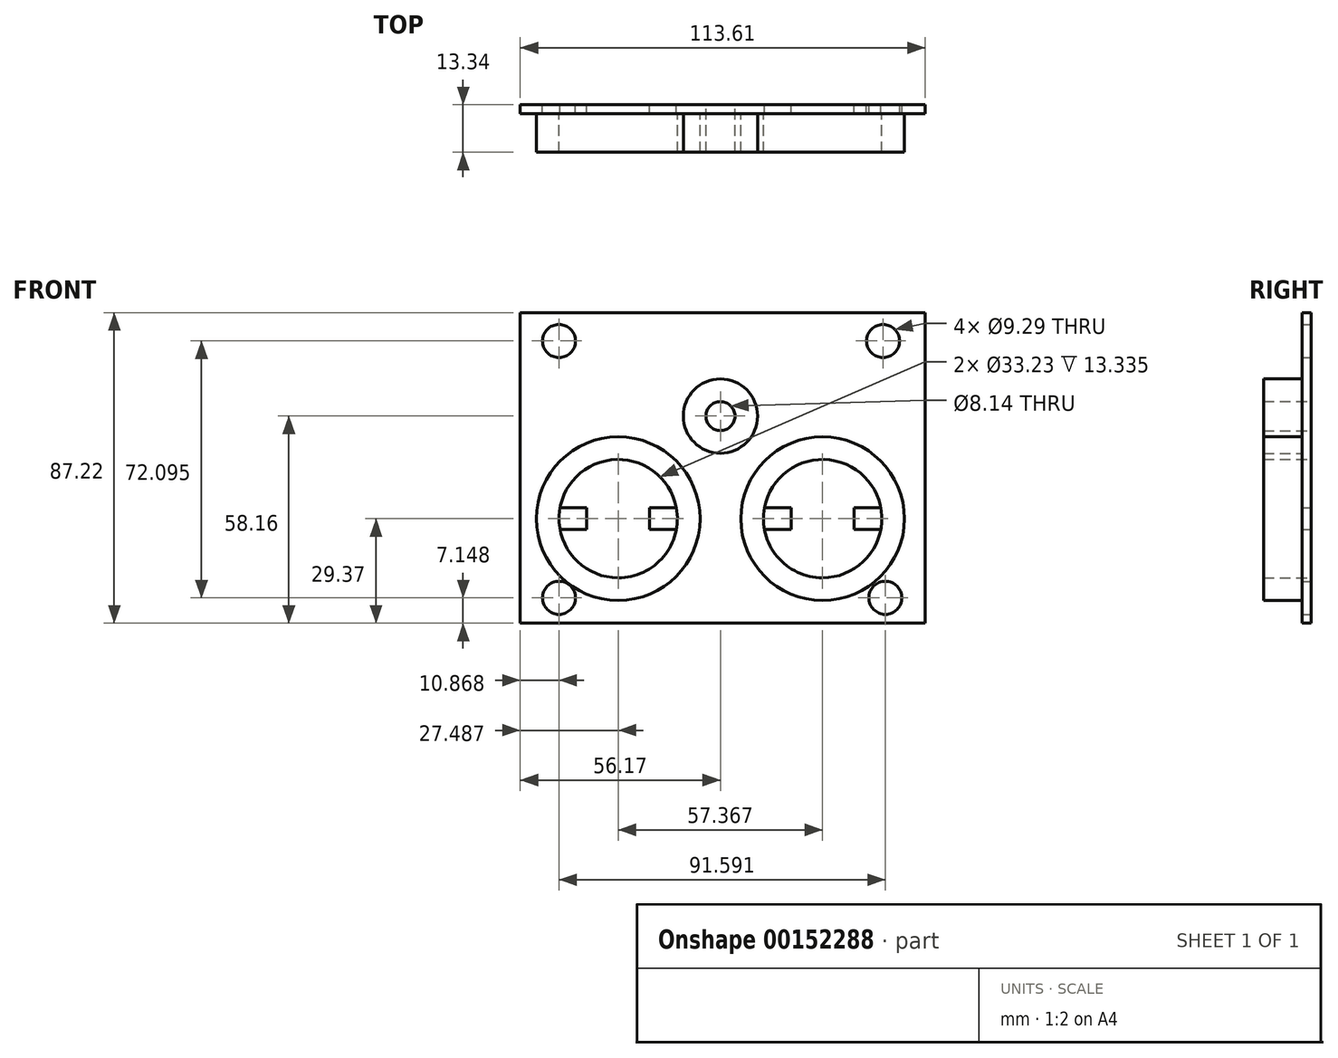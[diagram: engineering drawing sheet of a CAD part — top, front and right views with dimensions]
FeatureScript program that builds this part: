
annotation { "Feature Type Name" : "Feature", "Feature Type Description" : "" }
export const myFeature = defineFeature(function(context is Context, id is Id, definition is map)
    precondition{}
    {
        {
            var Q0;
            Q0=qCreatedBy(makeId("Front.planeOp"),FACE);
            cPlane(context, id + "F0", {"entities" : qUnion([Q0]), "cplaneType" : CPlaneType.OFFSET, "offset" : 76.2 * mm, "width" : 152.4 * mm, "height" : 152.4 * mm});
        }
        {
            var Q0;
            Q0=qCreatedBy(id+"F0.planeOp",FACE);
            var sketch = newSketch(context, id + "F1", { "sketchPlane" : qUnion([Q0])});
            skCircle(sketch, "E0", {"center": v(-28.68, 0) * mm, "radius": 20.32 * mm, "construction": true});
            skCircle(sketch, "E1", {"center": v(0, 28.8) * mm, "radius": 20.32 * mm, "construction": true});
            skCircle(sketch, "E2", {"center": v(28.68, 0) * mm, "radius": 20.32 * mm, "construction": true});
            skLineSegment(sketch, "E3.bottom", {"start": v(-56.17, 57.85) * mm, "end": v(57.44, 57.85) * mm});
            skLineSegment(sketch, "E3.top", {"start": v(-56.17, -29.37) * mm, "end": v(57.44, -29.37) * mm});
            skLineSegment(sketch, "E3.left", {"start": v(-56.17, 57.85) * mm, "end": v(-56.17, -29.37) * mm});
            skLineSegment(sketch, "E3.right", {"start": v(57.44, 57.85) * mm, "end": v(57.44, -29.37) * mm});
            skCircle(sketch, "E4", {"center": v(28.68, 0) * mm, "radius": 16.61 * mm});
            skCircle(sketch, "E5", {"center": v(-28.68, 0) * mm, "radius": 16.61 * mm});
            skCircle(sketch, "E6", {"center": v(0, 28.8) * mm, "radius": 4.07 * mm});
            skCircle(sketch, "E7", {"center": v(-28.68, 0) * mm, "radius": 4.07 * mm});
            skCircle(sketch, "E8", {"center": v(28.68, 0) * mm, "radius": 4.07 * mm});
            skCircle(sketch, "E9", {"center": v(28.68, 0) * mm, "radius": 7.31 * mm});
            skCircle(sketch, "E10", {"center": v(-28.68, 0) * mm, "radius": 7.31 * mm});
            skCircle(sketch, "E11", {"center": v(-45.3, 49.87) * mm, "radius": 4.65 * mm});
            skCircle(sketch, "E12", {"center": v(45.64, 49.87) * mm, "radius": 4.65 * mm});
            skCircle(sketch, "E13", {"center": v(46.29, -22.22) * mm, "radius": 4.65 * mm});
            skCircle(sketch, "E14", {"center": v(-45.3, -22.22) * mm, "radius": 4.65 * mm});
            skLineSegment(sketch, "E15.bottom", {"start": v(37.53, 3.04) * mm, "end": v(45.02, 3.04) * mm});
            skLineSegment(sketch, "E15.top", {"start": v(37.53, -3.04) * mm, "end": v(45.02, -3.04) * mm});
            skLineSegment(sketch, "E15.left", {"start": v(37.53, 3.04) * mm, "end": v(37.53, -3.04) * mm});
            skLineSegment(sketch, "E16", {"start": v(37.53, 0) * mm, "end": v(28.68, 0) * mm, "construction": true});
            skLineSegment(sketch, "E17", {"start": v(28.68, 0) * mm, "end": v(28.68, 20.32) * mm, "construction": true});
            skLineSegment(sketch, "E18", {"start": v(0, 0) * mm, "end": v(0, 28.8) * mm, "construction": true});
            skLineSegment(sketch, "E19", {"start": v(-28.68, 0) * mm, "end": v(0, 0) * mm, "construction": true});
            skLineSegment(sketch, "E20", {"start": v(0, 0) * mm, "end": v(28.68, 0) * mm, "construction": true});
            skSolve(sketch);
        }
        {
            var Q0;
            Q0=qCreatedBy(makeId("Front.planeOp"),FACE);
            var sketch = newSketch(context, id + "F2", { "sketchPlane" : qUnion([Q0])});
            skLineSegment(sketch, "E21.bottom", {"start": v(-56.17, -29.37) * mm, "end": v(57.44, -29.37) * mm});
            skLineSegment(sketch, "E21.top", {"start": v(-56.17, 57.85) * mm, "end": v(57.44, 57.85) * mm});
            skLineSegment(sketch, "E21.left", {"start": v(-56.17, -29.37) * mm, "end": v(-56.17, 57.85) * mm});
            skLineSegment(sketch, "E21.right", {"start": v(57.44, -29.37) * mm, "end": v(57.44, 57.85) * mm});
            skCircle(sketch, "E22", {"center": v(-28.68, 0) * mm, "radius": 16.61 * mm});
            skCircle(sketch, "E23", {"center": v(28.68, 0) * mm, "radius": 16.61 * mm});
            skCircle(sketch, "E24", {"center": v(0, 28.8) * mm, "radius": 4.07 * mm});
            skCircle(sketch, "E25.0", {"center": v(-28.68, 0) * mm, "radius": 22.96 * mm});
            skCircle(sketch, "E26.0", {"center": v(0, 28.8) * mm, "radius": 10.42 * mm});
            skCircle(sketch, "E27.0", {"center": v(28.68, 0) * mm, "radius": 22.96 * mm});
            skCircle(sketch, "E28", {"center": v(45.64, 49.87) * mm, "radius": 4.65 * mm});
            skCircle(sketch, "E29", {"center": v(-45.3, 49.87) * mm, "radius": 4.65 * mm});
            skCircle(sketch, "E30", {"center": v(-45.3, -22.22) * mm, "radius": 4.65 * mm});
            skCircle(sketch, "E31", {"center": v(46.29, -22.22) * mm, "radius": 4.65 * mm});
            skSolve(sketch);
        }
        {
            var Q0;
            Q0=makeQuery(id+"F2.imprint","IMPRINT",FACE,{"disambiguationData":[TD([[makeQuery(id+"F2.imprint","IMPRINT",EDGE,{"derivedFrom":sQuery(id+"F2.wireOp",EDGE,"E21.bottom")}),1.0]])]});
            var Q1;
            Q1=makeQuery(id+"F2.imprint","IMPRINT",FACE,{"disambiguationData":[TD([[makeQuery(id+"F2.imprint","IMPRINT",EDGE,{"derivedFrom":sQuery(id+"F2.wireOp",EDGE,"E22")}),-1.0]])]});
            var Q2;
            Q2=makeQuery(id+"F2.imprint","IMPRINT",FACE,{"disambiguationData":[TD([[makeQuery(id+"F2.imprint","IMPRINT",EDGE,{"derivedFrom":sQuery(id+"F2.wireOp",EDGE,"E24")}),-1.0]])]});
            var Q3;
            Q3=makeQuery(id+"F2.imprint","IMPRINT",FACE,{"disambiguationData":[TD([[makeQuery(id+"F2.imprint","IMPRINT",EDGE,{"derivedFrom":sQuery(id+"F2.wireOp",EDGE,"E23")}),-1.0]])]});
            var Q4;
            Q4=sQuery(id+"F2.wireOp",EDGE,"E21.top");
            extrude(context, id + "F3", {"entities" : qUnion([Q0, Q1, Q2, Q3]), "surfaceEntities" : qUnion([Q4]), "depth" : 2.54 * mm});
        }
        {
            var Q0;
            Q0=makeQuery(id+"F2.imprint","IMPRINT",FACE,{"disambiguationData":[TD([[makeQuery(id+"F2.imprint","IMPRINT",EDGE,{"derivedFrom":sQuery(id+"F2.wireOp",EDGE,"E24")}),-1.0]])]});
            var Q1;
            Q1=makeQuery(id+"F2.imprint","IMPRINT",FACE,{"disambiguationData":[TD([[makeQuery(id+"F2.imprint","IMPRINT",EDGE,{"derivedFrom":sQuery(id+"F2.wireOp",EDGE,"E23")}),-1.0]])]});
            var Q2;
            Q2=makeQuery(id+"F2.imprint","IMPRINT",FACE,{"disambiguationData":[TD([[makeQuery(id+"F2.imprint","IMPRINT",EDGE,{"derivedFrom":sQuery(id+"F2.wireOp",EDGE,"E22")}),-1.0]])]});
            extrude(context, id + "F4", {"entities" : qUnion([Q0, Q1, Q2]), "operationType" : NewBodyOperationType.ADD, "depth" : 13.33 * mm});
        }
        {
            var Q0;
            Q0=makeQuery(id+"F3.opExtrude","CAP_FACE",FACE,{"disambiguationData":[OSD([sQuery(id+"F2.wireOp",EDGE,"E21.bottom"),sQuery(id+"F2.wireOp",EDGE,"E21.top"),sQuery(id+"F2.wireOp",EDGE,"E21.left"),sQuery(id+"F2.wireOp",EDGE,"E21.right"),sQuery(id+"F2.wireOp",EDGE,"E22"),sQuery(id+"F2.wireOp",EDGE,"E23"),sQuery(id+"F2.wireOp",EDGE,"E24"),sQuery(id+"F2.wireOp",EDGE,"E28"),sQuery(id+"F2.wireOp",EDGE,"E29"),sQuery(id+"F2.wireOp",EDGE,"E30"),sQuery(id+"F2.wireOp",EDGE,"E31")])],"isStart":true});
            var sketch = newSketch(context, id + "F5", { "sketchPlane" : qUnion([Q0])});
            skLineSegment(sketch, "E32.bottom", {"start": v(-19.84, 3.04) * mm, "end": v(-12.35, 3.04) * mm});
            skLineSegment(sketch, "E32.top", {"start": v(-19.84, -3.04) * mm, "end": v(-12.35, -3.04) * mm});
            skLineSegment(sketch, "E32.left", {"start": v(-37.53, 3.04) * mm, "end": v(-37.53, -3.04) * mm});
            skArc(sketch, "E33", {"start": v(-12.35, -3.04) * mm, "mid": v(-12.07, 0) * mm, "end": v(-12.35, 3.04) * mm});
            skArc(sketch, "E34.MirrorCS", {"start": v(-45.02, -3.04) * mm, "mid": v(-45.3, 0) * mm, "end": v(-45.02, 3.04) * mm});
            skLineSegment(sketch, "E35.MirrorCS", {"start": v(-37.53, 3.04) * mm, "end": v(-45.02, 3.04) * mm});
            skLineSegment(sketch, "E36.MirrorCS", {"start": v(-37.53, -3.04) * mm, "end": v(-45.02, -3.04) * mm});
            skLineSegment(sketch, "E37.MirrorCS", {"start": v(-19.84, 3.04) * mm, "end": v(-19.84, -3.04) * mm});
            skLineSegment(sketch, "E38.MirrorCS", {"start": v(37.53, 3.04) * mm, "end": v(37.53, -3.04) * mm});
            skLineSegment(sketch, "E39.MirrorCS", {"start": v(37.53, -3.04) * mm, "end": v(45.02, -3.04) * mm});
            skArc(sketch, "E40.MirrorCS", {"start": v(45.02, -3.04) * mm, "mid": v(45.3, 0) * mm, "end": v(45.02, 3.04) * mm});
            skArc(sketch, "E41.MirrorCS", {"start": v(12.35, -3.04) * mm, "mid": v(12.07, 0) * mm, "end": v(12.35, 3.04) * mm});
            skLineSegment(sketch, "E42.MirrorCS", {"start": v(19.84, 3.04) * mm, "end": v(19.84, -3.04) * mm});
            skLineSegment(sketch, "E43.MirrorCS", {"start": v(37.53, 3.04) * mm, "end": v(45.02, 3.04) * mm});
            skLineSegment(sketch, "E44.MirrorCS", {"start": v(19.84, 3.04) * mm, "end": v(12.35, 3.04) * mm});
            skLineSegment(sketch, "E45.MirrorCS", {"start": v(19.84, -3.04) * mm, "end": v(12.35, -3.04) * mm});
            skSolve(sketch);
        }
        {
            var Q0;
            Q0 = qSketchRegion(id + "F5", true);
            extrude(context, id + "F6", {"entities" : qUnion([Q0]), "operationType" : NewBodyOperationType.ADD, "oppositeDirection" : true, "depth" : 2.54 * mm});
        }
    });
